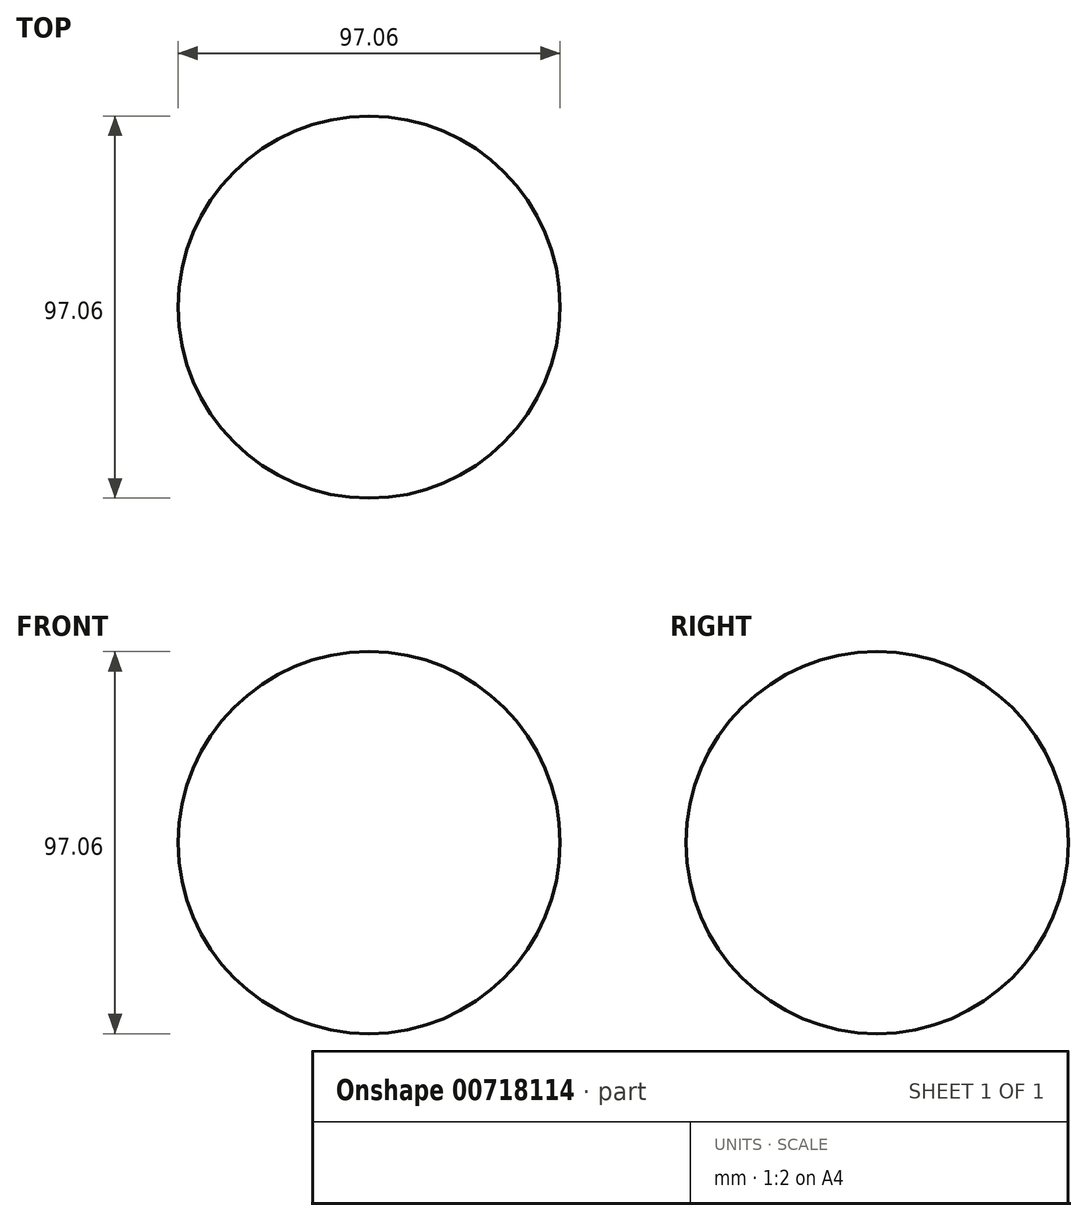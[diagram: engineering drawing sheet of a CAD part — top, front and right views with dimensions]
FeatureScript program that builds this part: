
annotation { "Feature Type Name" : "Feature", "Feature Type Description" : "" }
export const myFeature = defineFeature(function(context is Context, id is Id, definition is map)
    precondition{}
    {
        {
            var Q0;
            Q0=qCreatedBy(makeId("Top.planeOp"),FACE);
            var sketch = newSketch(context, id + "F0", { "sketchPlane" : qUnion([Q0])});
            skCircle(sketch, "E0", {"center": v(0, 0) * mm, "radius": 48.53 * mm});
            skLineSegment(sketch, "E1", {"start": v(0, 48.53) * mm, "end": v(0, -48.53) * mm});
            skSolve(sketch);
        }
        {
            var Q0;
            {var subQ0=sQuery(id+"F0.wireOp",EDGE,"E1");Q0=makeQuery(id+"F0.imprint","IMPRINT",FACE,{"disambiguationData":[TD([[makeQuery(id+"F0.imprint","IMPRINT",EDGE,{"derivedFrom":subQ0}),1.0]])]});}
            var Q1;
            Q1=sQuery(id+"F0.wireOp",EDGE,"E1");
            revolve(context, id + "F1", {"surfaceOperationType" : NewSurfaceOperationType.NEW, "entities" : qUnion([Q0]), "axis" : qUnion([Q1]), "revolveType" : RevolveType.FULL});
        }
    });
